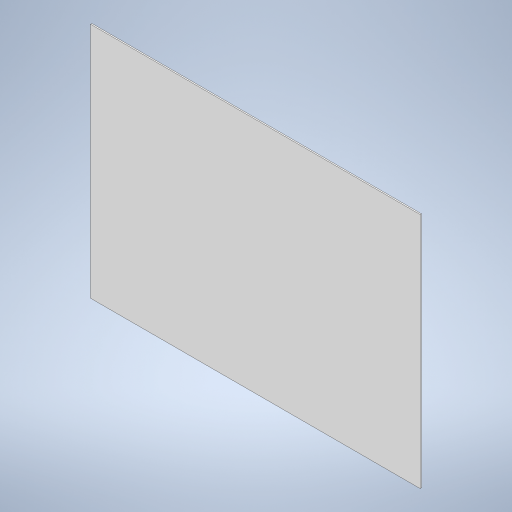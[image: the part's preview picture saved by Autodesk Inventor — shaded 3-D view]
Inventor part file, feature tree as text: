
AUTODESK INVENTOR PART (.ipt)
format: ipt  version: 2023 (Build 270158000, 158)  size: 188,928 bytes
history: native  units: mm
features: extrude x1, sketch x1
ambient origin geometry x8: Origin, YZ Plane, XZ Plane, XY Plane, X Axis, Y Axis, Z Axis, Center Point
bodies: Solid1 (feature_tree)
feature tree (2):
  extrude  "Extrusion1"  Depth=540.0mm
  sketch  "Sketch1"  dims[d0=750.0mm d1=540.0mm d2=3.0mm d3=0.0mm]
